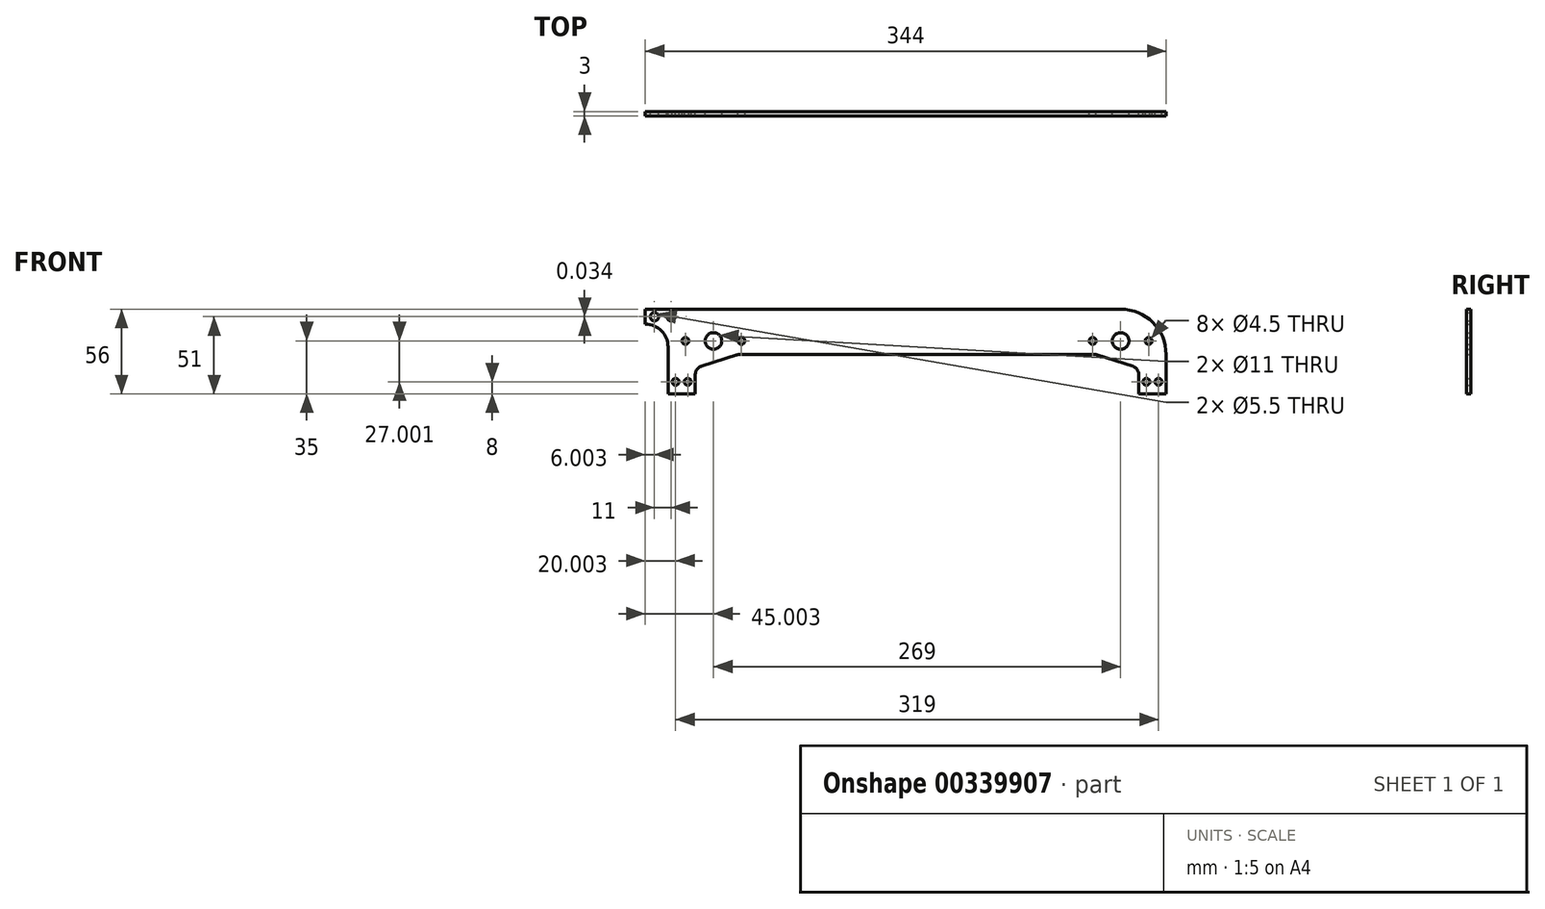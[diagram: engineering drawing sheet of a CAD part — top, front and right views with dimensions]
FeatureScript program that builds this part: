
annotation { "Feature Type Name" : "Feature", "Feature Type Description" : "" }
export const myFeature = defineFeature(function(context is Context, id is Id, definition is map)
    precondition{}
    {
        {
            var Q0;
            Q0=qCreatedBy(makeId("Front.planeOp"),FACE);
            var sketch = newSketch(context, id + "F0", { "sketchPlane" : qUnion([Q0])});
            skLineSegment(sketch, "E0.bottom", {"start": v(-101.58, 30) * mm, "end": v(167.42, 30) * mm});
            skLineSegment(sketch, "E0.left", {"start": v(-131.58, 0) * mm, "end": v(-131.58, -26) * mm});
            skLineSegment(sketch, "E0.right", {"start": v(197.42, 0) * mm, "end": v(197.42, -26) * mm});
            skLineSegment(sketch, "E1", {"start": v(-113.58, -26) * mm, "end": v(-113.58, -26) * mm});
            skLineSegment(sketch, "E2", {"start": v(-113.58, 0) * mm, "end": v(149.42, 0) * mm});
            skLineSegment(sketch, "E3", {"start": v(179.42, -26) * mm, "end": v(179.42, -26) * mm});
            skLineSegment(sketch, "E4", {"start": v(-131.58, -26) * mm, "end": v(-113.58, -26) * mm});
            skLineSegment(sketch, "E5", {"start": v(179.42, -26) * mm, "end": v(197.42, -26) * mm});
            skPoint(sketch, "E6.visualSharp", {"position": v(-113.58, 0) * mm});
            skPoint(sketch, "E7.visualSharp", {"position": v(179.42, 0) * mm});
            skPoint(sketch, "E8.visualSharp", {"position": v(-131.58, 30) * mm});
            skArc(sketch, "E8.filletArc", {"start": v(-101.58, 30) * mm, "mid": v(-122.8, 21.21) * mm, "end": v(-131.58, 0) * mm});
            skPoint(sketch, "E9.visualSharp", {"position": v(197.42, 30) * mm});
            skArc(sketch, "E9.filletArc", {"start": v(197.42, 0) * mm, "mid": v(188.64, 21.21) * mm, "end": v(167.42, 30) * mm});
            skLineSegment(sketch, "E10", {"start": v(-101.58, 30) * mm, "end": v(-101.58, 0) * mm, "construction": true});
            skCircle(sketch, "E11", {"center": v(-101.58, 9) * mm, "radius": 9.5 * mm, "construction": true});
            skCircle(sketch, "E12", {"center": v(-101.58, 9) * mm, "radius": 5.5 * mm});
            skLineSegment(sketch, "E13", {"start": v(167.42, 0) * mm, "end": v(167.42, 30) * mm, "construction": true});
            skCircle(sketch, "E14", {"center": v(167.42, 9) * mm, "radius": 9.5 * mm, "construction": true});
            skCircle(sketch, "E15", {"center": v(167.42, 9) * mm, "radius": 5.5 * mm});
            skLineSegment(sketch, "E16", {"start": v(-131.58, -18) * mm, "end": v(-111.07, -18) * mm, "construction": true});
            skCircle(sketch, "E17", {"center": v(192.42, -18) * mm, "radius": 2.25 * mm});
            skCircle(sketch, "E18", {"center": v(184.42, -18) * mm, "radius": 2.25 * mm});
            skCircle(sketch, "E19", {"center": v(-126.58, -18) * mm, "radius": 2.25 * mm});
            skCircle(sketch, "E20", {"center": v(-118.58, -18) * mm, "radius": 2.25 * mm});
            skLineSegment(sketch, "E21", {"start": v(184.42, -18) * mm, "end": v(197.42, -18) * mm, "construction": true});
            skLineSegment(sketch, "E22", {"start": v(-113.58, -26) * mm, "end": v(179.42, -26) * mm, "construction": true});
            skCircle(sketch, "E23", {"center": v(167.42, 9) * mm, "radius": 18.5 * mm, "construction": true});
            skLineSegment(sketch, "E24", {"start": v(167.42, 9) * mm, "end": v(167.42, -26) * mm, "construction": true});
            skLineSegment(sketch, "E25", {"start": v(-49.58, 9) * mm, "end": v(190.6, 9) * mm, "construction": true});
            skCircle(sketch, "E26", {"center": v(148.92, 9) * mm, "radius": 2.25 * mm});
            skCircle(sketch, "E27", {"center": v(185.92, 9) * mm, "radius": 2.25 * mm});
            skCircle(sketch, "E28", {"center": v(-101.58, 9) * mm, "radius": 18.5 * mm, "construction": true});
            skCircle(sketch, "E29", {"center": v(-83.08, 9) * mm, "radius": 2.25 * mm});
            skCircle(sketch, "E30", {"center": v(-120.08, 9) * mm, "radius": 2.25 * mm});
            skLineSegment(sketch, "E31", {"start": v(-113.58, -26) * mm, "end": v(-113.58, -18) * mm});
            skLineSegment(sketch, "E32", {"start": v(179.42, -26) * mm, "end": v(179.42, -18) * mm});
            skLineSegment(sketch, "E33", {"start": v(-113.58, -18) * mm, "end": v(-113.58, 0) * mm});
            skLineSegment(sketch, "E34", {"start": v(-113.58, -9) * mm, "end": v(-113.58, -9) * mm});
            skLineSegment(sketch, "E35", {"start": v(179.42, -18) * mm, "end": v(179.42, 0) * mm});
            skLineSegment(sketch, "E36", {"start": v(179.42, -9) * mm, "end": v(179.42, -9) * mm});
            skLineSegment(sketch, "E37", {"start": v(179.42, -9) * mm, "end": v(151.26, 0) * mm});
            skLineSegment(sketch, "E38", {"start": v(-113.58, -9) * mm, "end": v(-85.41, 0) * mm});
            skLineSegment(sketch, "E39", {"start": v(149.42, 0) * mm, "end": v(151.26, 0) * mm});
            skLineSegment(sketch, "E40", {"start": v(-101.58, 30) * mm, "end": v(-146.58, 30) * mm});
            skLineSegment(sketch, "E41", {"start": v(-146.58, 30) * mm, "end": v(-146.58, 20) * mm});
            skLineSegment(sketch, "E42", {"start": v(-131.58, 0) * mm, "end": v(-131.58, 20) * mm});
            skLineSegment(sketch, "E43", {"start": v(-131.58, 20) * mm, "end": v(-146.58, 20) * mm});
            skCircle(sketch, "E44", {"center": v(-140.58, 25) * mm, "radius": 2.75 * mm});
            skPoint(sketch, "E44.centerSnap0", {"position": v(-146.58, 25) * mm});
            skCircle(sketch, "E45", {"center": v(-129.58, 25.03) * mm, "radius": 2.75 * mm});
            skSolve(sketch);
        }
        {
            var Q0;
            Q0 = qSketchRegion(id + "F0", true);
            extrude(context, id + "F1", {"entities" : qUnion([Q0]), "depth" : 3 * mm});
        }
        {
            var Q0;
            Q0=makeQuery(id+"F1.opExtrude","SWEPT_EDGE",EDGE,{"disambiguationData":[OSD([sQuery(id+"F0.wireOp",EDGE,"E33"),sQuery(id+"F0.wireOp",EDGE,"E34")])]});
            var Q1;
            Q1=makeQuery(id+"F1.opExtrude","SWEPT_EDGE",EDGE,{"disambiguationData":[OSD([sQuery(id+"F0.wireOp",EDGE,"E2"),sQuery(id+"F0.wireOp",EDGE,"E38")])]});
            var Q2;
            Q2=makeQuery(id+"F1.opExtrude","SWEPT_EDGE",EDGE,{"disambiguationData":[OSD([sQuery(id+"F0.wireOp",EDGE,"E34"),sQuery(id+"F0.wireOp",EDGE,"E38")])]});
            var Q3;
            Q3=makeQuery(id+"F1.opExtrude","SWEPT_EDGE",EDGE,{"disambiguationData":[OSD([sQuery(id+"F0.wireOp",EDGE,"E37"),sQuery(id+"F0.wireOp",EDGE,"E39")])]});
            var Q4;
            Q4=makeQuery(id+"F1.opExtrude","SWEPT_EDGE",EDGE,{"disambiguationData":[OSD([sQuery(id+"F0.wireOp",EDGE,"E36"),sQuery(id+"F0.wireOp",EDGE,"E37")])]});
            var Q5;
            Q5=makeQuery(id+"F1.opExtrude","SWEPT_EDGE",EDGE,{"disambiguationData":[OSD([sQuery(id+"F0.wireOp",EDGE,"E35"),sQuery(id+"F0.wireOp",EDGE,"E36")])]});
            fillet(context, id + "F2", {"entities" : qUnion([Q0, Q1, Q2, Q3, Q4, Q5]), "radius" : 6 * mm, "tangentPropagation" : true, "allowEdgeOverflow" : false});
        }
        {
            var Q0;
            Q0=makeQuery(id+"F1.opExtrude","SWEPT_EDGE",EDGE,{"disambiguationData":[OSD([sQuery(id+"F0.wireOp",EDGE,"E42"),sQuery(id+"F0.wireOp",EDGE,"E43")])]});
            fillet(context, id + "F3", {"entities" : qUnion([Q0]), "radius" : 15 * mm, "tangentPropagation" : true, "allowEdgeOverflow" : false});
        }
    });
